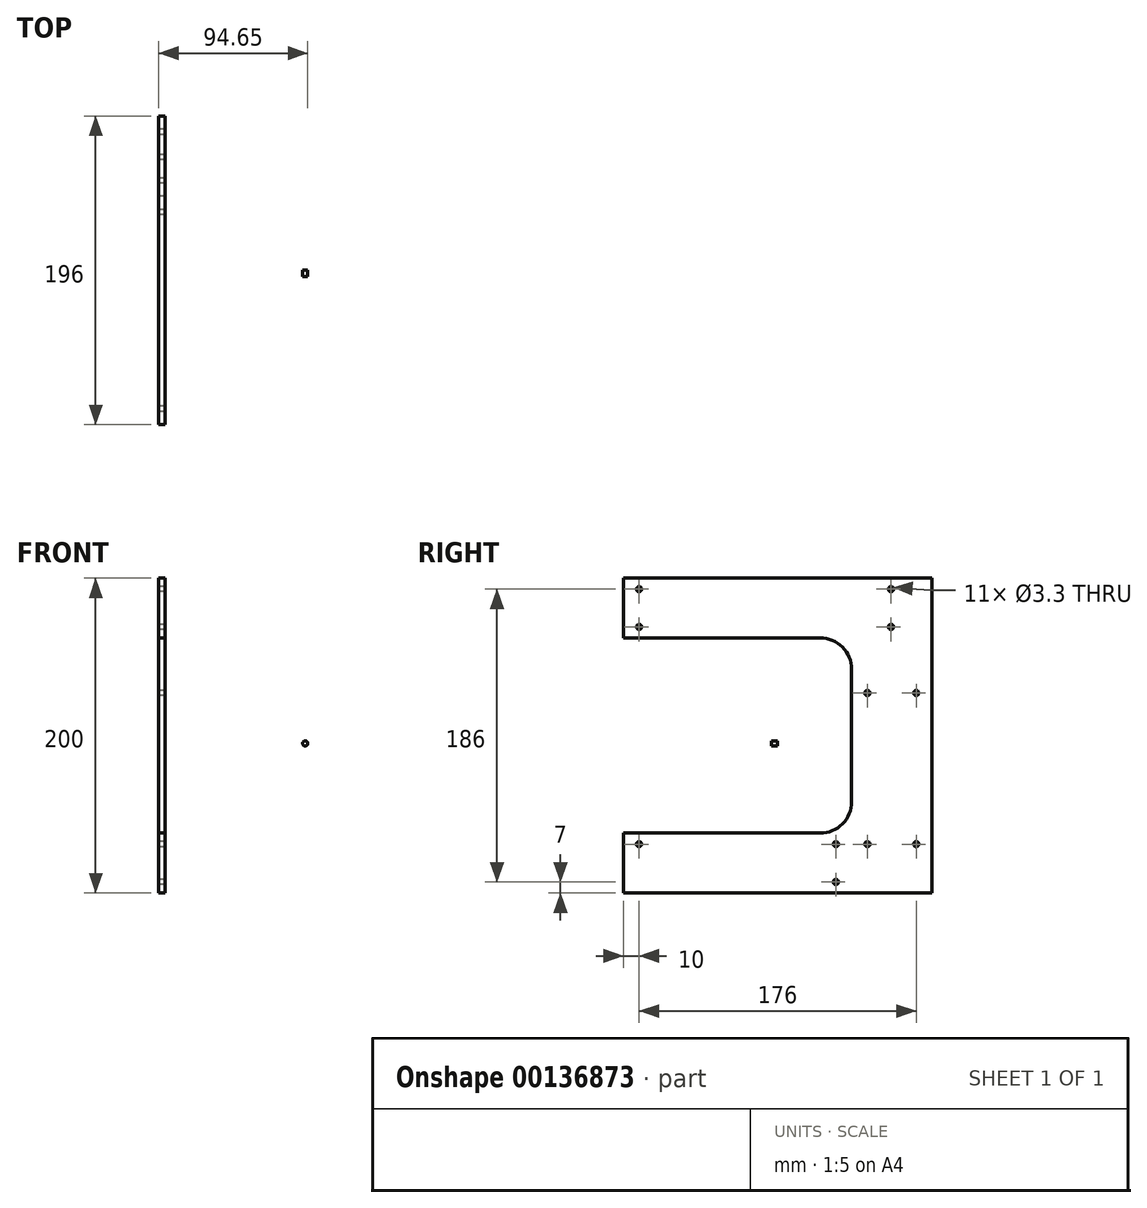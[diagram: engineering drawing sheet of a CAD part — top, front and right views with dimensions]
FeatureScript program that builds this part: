
annotation { "Feature Type Name" : "Feature", "Feature Type Description" : "" }
export const myFeature = defineFeature(function(context is Context, id is Id, definition is map)
    precondition{}
    {
        {
            var Q0;
            Q0=qCreatedBy(makeId("Front.planeOp"),FACE);
            var sketch = newSketch(context, id + "F0", { "sketchPlane" : qUnion([Q0])});
            skCircle(sketch, "E0", {"center": v(93, -78.07) * mm, "radius": 1.65 * mm});
            skCircle(sketch, "E1", {"center": v(-93, -78.07) * mm, "radius": 1.65 * mm});
            skCircle(sketch, "E2", {"center": v(-93, -68.07) * mm, "radius": 1.65 * mm});
            skCircle(sketch, "E3", {"center": v(93, -68.07) * mm, "radius": 1.65 * mm});
            skLineSegment(sketch, "E4", {"start": v(100, -54.07) * mm, "end": v(-100, -54.07) * mm});
            skLineSegment(sketch, "E5", {"start": v(100, -92.07) * mm, "end": v(100, -54.07) * mm});
            skLineSegment(sketch, "E6", {"start": v(-100, -92.07) * mm, "end": v(100, -92.07) * mm});
            skLineSegment(sketch, "E7", {"start": v(-100, -54.07) * mm, "end": v(-100, -92.07) * mm});
            skCircle(sketch, "E8", {"center": v(93, -5) * mm, "radius": 1.65 * mm});
            skCircle(sketch, "E9", {"center": v(-93, -5) * mm, "radius": 1.65 * mm});
            skCircle(sketch, "E10", {"center": v(-93, 5) * mm, "radius": 1.65 * mm});
            skCircle(sketch, "E11", {"center": v(93, 5) * mm, "radius": 1.65 * mm});
            skLineSegment(sketch, "E12", {"start": v(100, 19) * mm, "end": v(-100, 19) * mm});
            skLineSegment(sketch, "E13", {"start": v(100, -19) * mm, "end": v(100, 19) * mm});
            skLineSegment(sketch, "E14", {"start": v(-100, -19) * mm, "end": v(100, -19) * mm});
            skLineSegment(sketch, "E15", {"start": v(-100, 19) * mm, "end": v(-100, -19) * mm});
            skSolve(sketch);
        }
        {
            var Q0;
            Q0=makeQuery(id+"F0.imprint","IMPRINT",FACE,{"disambiguationData":[TD([[makeQuery(id+"F0.imprint","IMPRINT",EDGE,{"derivedFrom":sQuery(id+"F0.wireOp",EDGE,"E8")}),1.0]])]});
            extrude(context, id + "F1", {"entities" : qUnion([Q0]), "depth" : 4 * mm});
        }
        {
            var Q0;
            Q0=qCreatedBy(makeId("Right.planeOp"),FACE);
            var sketch = newSketch(context, id + "F2", { "sketchPlane" : qUnion([Q0])});
            skCircle(sketch, "E16", {"center": v(-88, -93) * mm, "radius": 1.65 * mm});
            skCircle(sketch, "E17", {"center": v(37, -93) * mm, "radius": 1.65 * mm});
            skCircle(sketch, "E18", {"center": v(88, -69) * mm, "radius": 1.65 * mm});
            skCircle(sketch, "E19", {"center": v(88, 27) * mm, "radius": 1.65 * mm});
            skCircle(sketch, "E20", {"center": v(72, 93) * mm, "radius": 1.65 * mm});
            skCircle(sketch, "E21", {"center": v(-88, 69) * mm, "radius": 1.65 * mm});
            skCircle(sketch, "E22", {"center": v(-88, 93) * mm, "radius": 1.65 * mm});
            skCircle(sketch, "E23", {"center": v(72, 69) * mm, "radius": 1.65 * mm});
            skCircle(sketch, "E24", {"center": v(57, 27) * mm, "radius": 1.65 * mm});
            skCircle(sketch, "E25", {"center": v(57, -69) * mm, "radius": 1.65 * mm});
            skCircle(sketch, "E26", {"center": v(37, -69) * mm, "radius": 1.65 * mm});
            skCircle(sketch, "E27", {"center": v(-88, -69) * mm, "radius": 1.65 * mm});
            skLineSegment(sketch, "E28", {"start": v(98, 100) * mm, "end": v(-98, 100) * mm});
            skLineSegment(sketch, "E29", {"start": v(98, -100) * mm, "end": v(98, 100) * mm});
            skLineSegment(sketch, "E30", {"start": v(-98, -100) * mm, "end": v(98, -100) * mm});
            skLineSegment(sketch, "E31", {"start": v(-98, -62) * mm, "end": v(-98, -100) * mm});
            skLineSegment(sketch, "E32", {"start": v(27, -62) * mm, "end": v(-98, -62) * mm});
            skLineSegment(sketch, "E33", {"start": v(47, 42) * mm, "end": v(47, -42) * mm});
            skLineSegment(sketch, "E34", {"start": v(-98, 62) * mm, "end": v(27, 62) * mm});
            skLineSegment(sketch, "E35", {"start": v(-98, 100) * mm, "end": v(-98, 62) * mm});
            skArc(sketch, "E36", {"start": v(27, -62) * mm, "mid": v(41.14, -56.14) * mm, "end": v(47, -42) * mm});
            skArc(sketch, "E37", {"start": v(47, 42) * mm, "mid": v(41.14, 56.14) * mm, "end": v(27, 62) * mm});
            skSolve(sketch);
        }
        {
            var Q0;
            Q0 = qSketchRegion(id + "F2", true);
            var Q1;
            Q1=makeQuery(id+"F2.imprint","IMPRINT",FACE,{"disambiguationData":[TD([[makeQuery(id+"F2.imprint","IMPRINT",EDGE,{"derivedFrom":sQuery(id+"F2.wireOp",EDGE,"E16")}),1.0]])]});
            extrude(context, id + "F3", {"entities" : qUnion([Q0, Q1]), "depth" : 4 * mm});
        }
    });
